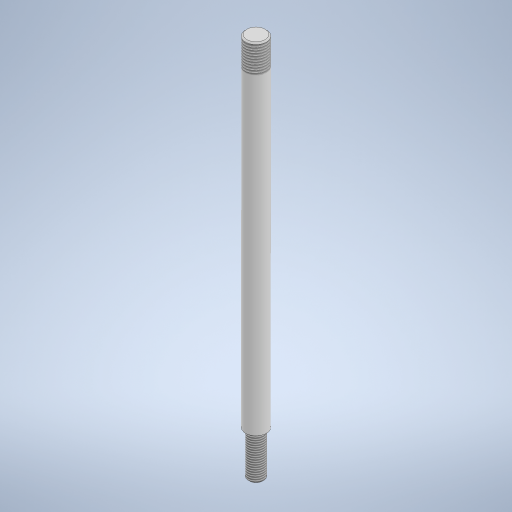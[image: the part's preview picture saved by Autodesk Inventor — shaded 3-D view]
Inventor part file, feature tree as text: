
AUTODESK INVENTOR PART (.ipt)
format: ipt  version: 2024.1 (Build 281209000, 209)  size: 256,512 bytes
history: native  units: mm
features: extrude x4, sketch x4, thread x2, chamfer x2, fillet x1
ambient origin geometry x8: Origin, YZ Plane, XZ Plane, XY Plane, X Axis, Y Axis, Z Axis, Center Point
bodies: Solid1 (feature_tree)
feature tree (13):
  extrude  "Extrusion1"  Depth=459.0mm TaperAngle=0.0deg
  extrude  "Extrusion2"  Depth=62.0mm TaperAngle=0.0deg
  fillet  "Fillet1"  Radius=2.0mm
  extrude  "Extrusion3"  Depth=12.7mm TaperAngle=0.0deg
  thread  "Thread2"  [1 undecoded]
  extrude  "Extrusion4"  Depth=2.0mm TaperAngle=0.0deg
  thread  "Thread3"  [1 undecoded]
  chamfer  "Chamfer1"  Distance=2.0mm Angle=45.0deg
  chamfer  "Chamfer2"  [1 undecoded]
  sketch  "Sketch1"  dims[d0=30.0mm d1=459.0mm d2=0.0mm]
  sketch  "Sketch2"  dims[d3=22.0mm d4=62.0mm d5=0.0mm d6=2.0mm]
  sketch  "Sketch3"  dims[d7=30.0mm d8=12.7mm d9=0.0mm d12=60.0mm d13=0.0mm]
  sketch  "Sketch4"  dims[d14=12.0mm d15=0.0mm d16=40.0mm d17=0.0mm d18=2.0mm d19=2.0mm d20=45.0deg d21=2.0mm d22=2.0mm d23=45.0deg]
note: 3 required parameter values undecoded (feature->parameter linkage not recoverable at this tier; creation-order binding heuristic only, values carry confidence <= 0.55)
